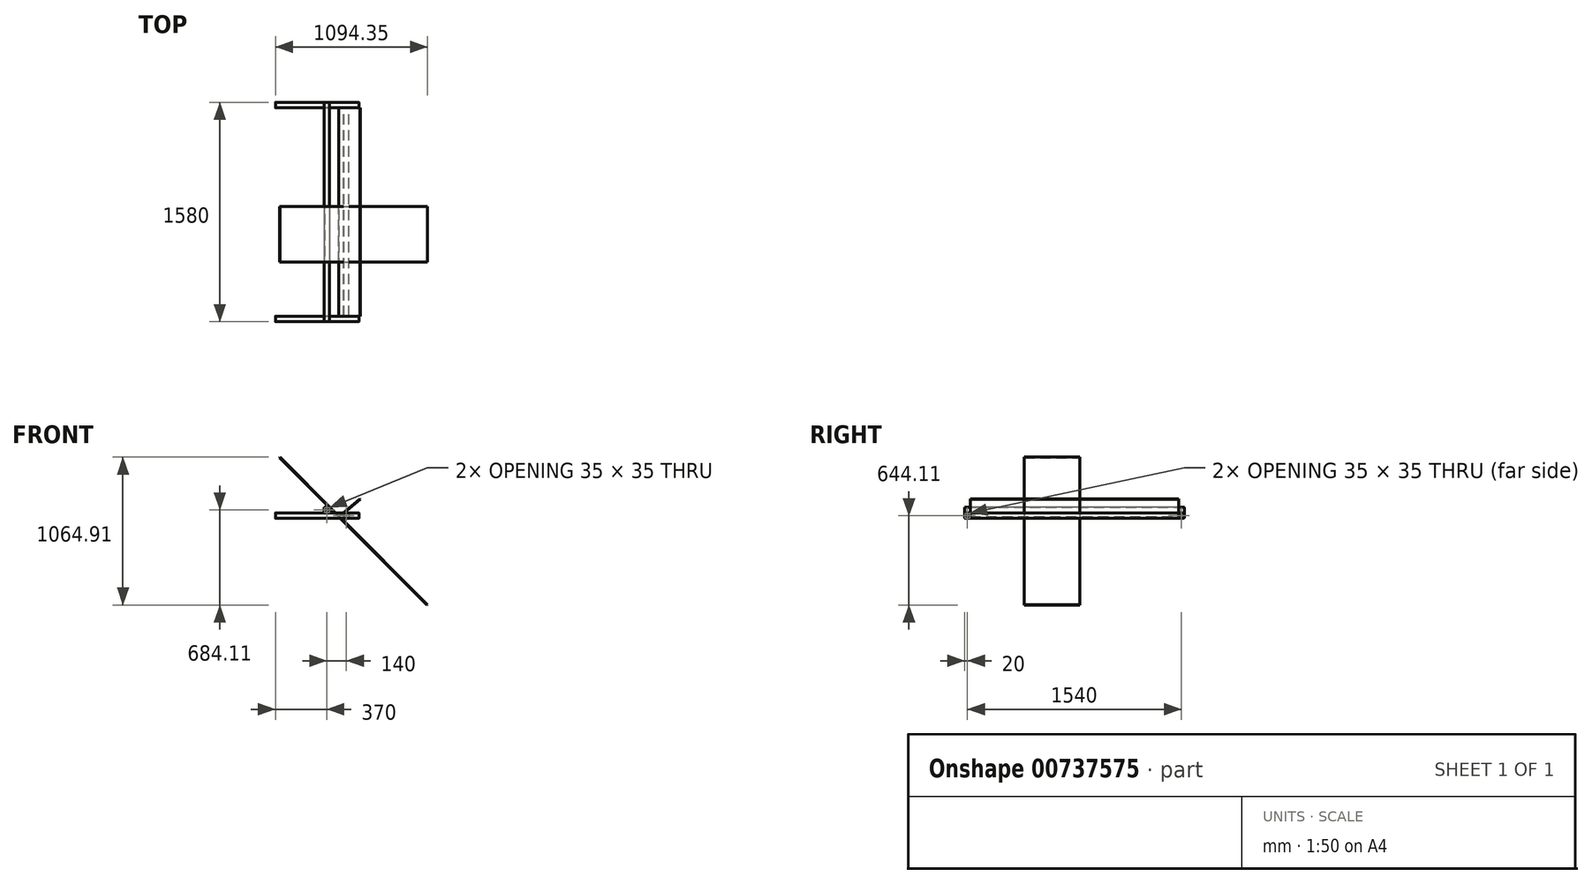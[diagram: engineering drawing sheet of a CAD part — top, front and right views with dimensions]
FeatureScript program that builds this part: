
annotation { "Feature Type Name" : "Feature", "Feature Type Description" : "" }
export const myFeature = defineFeature(function(context is Context, id is Id, definition is map)
    precondition{}
    {
        {
            var Q0;
            Q0=qCreatedBy(makeId("Right.planeOp"),FACE);
            var sketch = newSketch(context, id + "F0", { "sketchPlane" : qUnion([Q0])});
            skLineSegment(sketch, "E0.bottom", {"start": v(-504, 0) * mm, "end": v(-536, 0) * mm});
            skLineSegment(sketch, "E0.top", {"start": v(-504, 40) * mm, "end": v(-536, 40) * mm});
            skLineSegment(sketch, "E0.left", {"start": v(-500, 4) * mm, "end": v(-500, 36) * mm});
            skLineSegment(sketch, "E0.right", {"start": v(-540, 4) * mm, "end": v(-540, 36) * mm});
            skLineSegment(sketch, "E1.bottom", {"start": v(1004, 40) * mm, "end": v(1036, 40) * mm});
            skLineSegment(sketch, "E1.top", {"start": v(1004, 0) * mm, "end": v(1036, 0) * mm});
            skLineSegment(sketch, "E1.left", {"start": v(1000, 36) * mm, "end": v(1000, 4) * mm});
            skLineSegment(sketch, "E1.right", {"start": v(1040, 36) * mm, "end": v(1040, 4) * mm});
            skPoint(sketch, "E2.visualSharp", {"position": v(-500, 40) * mm});
            skArc(sketch, "E2.filletArc", {"start": v(-500, 36) * mm, "mid": v(-501.17, 38.83) * mm, "end": v(-504, 40) * mm});
            skPoint(sketch, "E3.visualSharp", {"position": v(-500, 0) * mm});
            skArc(sketch, "E3.filletArc", {"start": v(-504, 0) * mm, "mid": v(-501.17, 1.17) * mm, "end": v(-500, 4) * mm});
            skPoint(sketch, "E4.visualSharp", {"position": v(-540, 40) * mm});
            skArc(sketch, "E4.filletArc", {"start": v(-536, 40) * mm, "mid": v(-538.83, 38.83) * mm, "end": v(-540, 36) * mm});
            skPoint(sketch, "E5.visualSharp", {"position": v(-540, 0) * mm});
            skArc(sketch, "E5.filletArc", {"start": v(-540, 4) * mm, "mid": v(-538.83, 1.17) * mm, "end": v(-536, 0) * mm});
            skPoint(sketch, "E6.visualSharp", {"position": v(1040, 40) * mm});
            skArc(sketch, "E6.filletArc", {"start": v(1040, 36) * mm, "mid": v(1038.83, 38.83) * mm, "end": v(1036, 40) * mm});
            skPoint(sketch, "E7.visualSharp", {"position": v(1040, 0) * mm});
            skArc(sketch, "E7.filletArc", {"start": v(1036, 0) * mm, "mid": v(1038.83, 1.17) * mm, "end": v(1040, 4) * mm});
            skPoint(sketch, "E8.visualSharp", {"position": v(1000, 0) * mm});
            skArc(sketch, "E8.filletArc", {"start": v(1000, 4) * mm, "mid": v(1001.17, 1.17) * mm, "end": v(1004, 0) * mm});
            skPoint(sketch, "E9.visualSharp", {"position": v(1000, 40) * mm});
            skArc(sketch, "E9.filletArc", {"start": v(1004, 40) * mm, "mid": v(1001.17, 38.83) * mm, "end": v(1000, 36) * mm});
            skSolve(sketch);
        }
        {
            var Q0;
            Q0=makeQuery(id+"F0.imprint","IMPRINT",FACE,{"disambiguationData":[TD([[makeQuery(id+"F0.imprint","IMPRINT",EDGE,{"derivedFrom":sQuery(id+"F0.wireOp",EDGE,"E0.bottom")}),-1.0]])]});
            var Q1;
            Q1=makeQuery(id+"F0.imprint","IMPRINT",FACE,{"disambiguationData":[TD([[makeQuery(id+"F0.imprint","IMPRINT",EDGE,{"derivedFrom":sQuery(id+"F0.wireOp",EDGE,"E1.bottom")}),-1.0]])]});
            extrude(context, id + "F1", {"entities" : qUnion([Q0, Q1]), "endBound" : BoundingType.SYMMETRIC, "depth" : 600 * mm, "offsetDistance" : 25 * mm});
        }
        {
            var Q0;
            Q0=makeQuery(id+"F1.opExtrude","CAP_FACE",FACE,{"disambiguationData":[OSD([sQuery(id+"F0.wireOp",EDGE,"E0.bottom"),sQuery(id+"F0.wireOp",EDGE,"E0.top"),sQuery(id+"F0.wireOp",EDGE,"E0.left"),sQuery(id+"F0.wireOp",EDGE,"E0.right"),sQuery(id+"F0.wireOp",EDGE,"E2.filletArc"),sQuery(id+"F0.wireOp",EDGE,"E3.filletArc"),sQuery(id+"F0.wireOp",EDGE,"E4.filletArc"),sQuery(id+"F0.wireOp",EDGE,"E5.filletArc")])],"isStart":false});
            var Q1;
            Q1=makeQuery(id+"F1.opExtrude","CAP_FACE",FACE,{"disambiguationData":[OSD([sQuery(id+"F0.wireOp",EDGE,"E1.bottom"),sQuery(id+"F0.wireOp",EDGE,"E1.top"),sQuery(id+"F0.wireOp",EDGE,"E1.left"),sQuery(id+"F0.wireOp",EDGE,"E1.right"),sQuery(id+"F0.wireOp",EDGE,"E6.filletArc"),sQuery(id+"F0.wireOp",EDGE,"E7.filletArc"),sQuery(id+"F0.wireOp",EDGE,"E8.filletArc"),sQuery(id+"F0.wireOp",EDGE,"E9.filletArc")])],"isStart":false});
            var Q2;
            Q2=makeQuery(id+"F1.opExtrude","SWEPT_BODY",BODY,{"disambiguationData":[OSD([sQuery(id+"F0.wireOp",EDGE,"E0.bottom"),sQuery(id+"F0.wireOp",EDGE,"E0.top"),sQuery(id+"F0.wireOp",EDGE,"E0.left"),sQuery(id+"F0.wireOp",EDGE,"E0.right"),sQuery(id+"F0.wireOp",EDGE,"E2.filletArc"),sQuery(id+"F0.wireOp",EDGE,"E3.filletArc"),sQuery(id+"F0.wireOp",EDGE,"E4.filletArc"),sQuery(id+"F0.wireOp",EDGE,"E5.filletArc")])]});
            shell(context, id + "F2", {"entities" : qUnion([Q0, Q1]), "parts" : qUnion([Q2]), "thickness" : 2.5 * mm});
        }
        {
            var Q0;
            Q0=makeQuery(id+"F1.opExtrude","CAP_FACE",FACE,{"disambiguationData":[OSD([sQuery(id+"F0.wireOp",EDGE,"E0.bottom"),sQuery(id+"F0.wireOp",EDGE,"E0.top"),sQuery(id+"F0.wireOp",EDGE,"E0.left"),sQuery(id+"F0.wireOp",EDGE,"E0.right"),sQuery(id+"F0.wireOp",EDGE,"E2.filletArc"),sQuery(id+"F0.wireOp",EDGE,"E3.filletArc"),sQuery(id+"F0.wireOp",EDGE,"E4.filletArc"),sQuery(id+"F0.wireOp",EDGE,"E5.filletArc")])],"isStart":false});
            var sketch = newSketch(context, id + "F3", { "sketchPlane" : qUnion([Q0])});
            skArc(sketch, "E10.0.0", {"start": v(-502.5, 36) * mm, "mid": v(-502.94, 37.06) * mm, "end": v(-504, 37.5) * mm});
            skLineSegment(sketch, "E10.0.1", {"start": v(-504, 37.5) * mm, "end": v(-536, 37.5) * mm});
            skArc(sketch, "E10.0.2", {"start": v(-536, 37.5) * mm, "mid": v(-537.06, 37.06) * mm, "end": v(-537.5, 36) * mm});
            skLineSegment(sketch, "E10.0.3", {"start": v(-537.5, 36) * mm, "end": v(-537.5, 4) * mm});
            skArc(sketch, "E10.0.4", {"start": v(-537.5, 4) * mm, "mid": v(-537.06, 2.94) * mm, "end": v(-536, 2.5) * mm});
            skLineSegment(sketch, "E10.0.5", {"start": v(-536, 2.5) * mm, "end": v(-504, 2.5) * mm});
            skArc(sketch, "E10.0.6", {"start": v(-504, 2.5) * mm, "mid": v(-502.94, 2.94) * mm, "end": v(-502.5, 4) * mm});
            skLineSegment(sketch, "E10.0.7", {"start": v(-502.5, 4) * mm, "end": v(-502.5, 36) * mm});
            skArc(sketch, "E11.0.0", {"start": v(1002.5, 4) * mm, "mid": v(1002.94, 2.94) * mm, "end": v(1004, 2.5) * mm});
            skLineSegment(sketch, "E11.0.1", {"start": v(1004, 2.5) * mm, "end": v(1036, 2.5) * mm});
            skArc(sketch, "E11.0.2", {"start": v(1036, 2.5) * mm, "mid": v(1037.06, 2.94) * mm, "end": v(1037.5, 4) * mm});
            skLineSegment(sketch, "E11.0.3", {"start": v(1037.5, 4) * mm, "end": v(1037.5, 36) * mm});
            skArc(sketch, "E11.0.4", {"start": v(1037.5, 36) * mm, "mid": v(1037.06, 37.06) * mm, "end": v(1036, 37.5) * mm});
            skLineSegment(sketch, "E11.0.5", {"start": v(1036, 37.5) * mm, "end": v(1004, 37.5) * mm});
            skArc(sketch, "E11.0.6", {"start": v(1004, 37.5) * mm, "mid": v(1002.94, 37.06) * mm, "end": v(1002.5, 36) * mm});
            skLineSegment(sketch, "E11.0.7", {"start": v(1002.5, 36) * mm, "end": v(1002.5, 4) * mm});
            skSolve(sketch);
        }
        {
            var Q0;
            Q0=makeQuery(id+"F3.imprint","IMPRINT",FACE,{"disambiguationData":[TD([[makeQuery(id+"F3.imprint","IMPRINT",EDGE,{"derivedFrom":sQuery(id+"F3.wireOp",EDGE,"E11.0.0")}),1.0]])]});
            var Q1;
            Q1=makeQuery(id+"F3.imprint","IMPRINT",FACE,{"disambiguationData":[TD([[makeQuery(id+"F3.imprint","IMPRINT",EDGE,{"derivedFrom":sQuery(id+"F3.wireOp",EDGE,"E10.0.0")}),1.0]])]});
            extrude(context, id + "F4", {"entities" : qUnion([Q0, Q1]), "operationType" : NewBodyOperationType.REMOVE, "oppositeDirection" : true, "depth" : 1000 * mm, "offsetDistance" : 25 * mm});
        }
        {
            var Q0;
            Q0=makeQuery(id+"F1.opExtrude","SWEPT_FACE",FACE,{"disambiguationData":[OSD([sQuery(id+"F0.wireOp",EDGE,"E0.right")])]});
            var sketch = newSketch(context, id + "F5", { "sketchPlane" : qUnion([Q0])});
            skLineSegment(sketch, "E12.0", {"start": v(86, 40) * mm, "end": v(54, 40) * mm});
            skLineSegment(sketch, "E13.bottom", {"start": v(-147.4, 40) * mm, "end": v(-107.4, 40) * mm});
            skLineSegment(sketch, "E13.top", {"start": v(54, 80) * mm, "end": v(86, 80) * mm});
            skLineSegment(sketch, "E13.left", {"start": v(50, 44) * mm, "end": v(50, 76) * mm});
            skLineSegment(sketch, "E13.right", {"start": v(90, 44) * mm, "end": v(90, 76) * mm});
            skPoint(sketch, "E14.visualSharp", {"position": v(90, 80) * mm});
            skArc(sketch, "E14.filletArc", {"start": v(90, 76) * mm, "mid": v(88.83, 78.83) * mm, "end": v(86, 80) * mm});
            skPoint(sketch, "E15.newPointB", {"position": v(300, 40) * mm});
            skArc(sketch, "E15.filletArc", {"start": v(86, 40) * mm, "mid": v(88.83, 41.17) * mm, "end": v(90, 44) * mm});
            skPoint(sketch, "E16.visualSharp", {"position": v(50, 80) * mm});
            skArc(sketch, "E16.filletArc", {"start": v(54, 80) * mm, "mid": v(51.17, 78.83) * mm, "end": v(50, 76) * mm});
            skPoint(sketch, "E17.newPointB", {"position": v(-300, 40) * mm});
            skArc(sketch, "E17.filletArc", {"start": v(50, 44) * mm, "mid": v(51.17, 41.17) * mm, "end": v(54, 40) * mm});
            skLineSegment(sketch, "E18.bottom", {"start": v(54.5, 77.5) * mm, "end": v(85.5, 77.5) * mm});
            skLineSegment(sketch, "E18.top", {"start": v(54.5, 42.5) * mm, "end": v(85.5, 42.5) * mm});
            skLineSegment(sketch, "E18.left", {"start": v(52.5, 75.5) * mm, "end": v(52.5, 44.5) * mm});
            skLineSegment(sketch, "E18.right", {"start": v(87.5, 75.5) * mm, "end": v(87.5, 44.5) * mm});
            skPoint(sketch, "E19.visualSharp", {"position": v(52.5, 77.5) * mm});
            skArc(sketch, "E19.filletArc", {"start": v(54.5, 77.5) * mm, "mid": v(53.09, 76.91) * mm, "end": v(52.5, 75.5) * mm});
            skPoint(sketch, "E20.visualSharp", {"position": v(87.5, 77.5) * mm});
            skArc(sketch, "E20.filletArc", {"start": v(87.5, 75.5) * mm, "mid": v(86.91, 76.91) * mm, "end": v(85.5, 77.5) * mm});
            skPoint(sketch, "E21.visualSharp", {"position": v(87.5, 42.5) * mm});
            skArc(sketch, "E21.filletArc", {"start": v(85.5, 42.5) * mm, "mid": v(86.91, 43.09) * mm, "end": v(87.5, 44.5) * mm});
            skPoint(sketch, "E22.visualSharp", {"position": v(52.5, 42.5) * mm});
            skArc(sketch, "E22.filletArc", {"start": v(52.5, 44.5) * mm, "mid": v(53.09, 43.09) * mm, "end": v(54.5, 42.5) * mm});
            skSolve(sketch);
        }
        {
            var Q0;
            Q0=makeQuery(id+"F5.imprint","IMPRINT",FACE,{"disambiguationData":[TD([[makeQuery(id+"F5.imprint","IMPRINT",EDGE,{"derivedFrom":sQuery(id+"F5.wireOp",EDGE,"E13.top")}),-1.0]])]});
            var Q1;
            Q1=makeQuery(id+"F1.opExtrude","SWEPT_FACE",FACE,{"disambiguationData":[OSD([sQuery(id+"F0.wireOp",EDGE,"E1.right")])]});
            extrude(context, id + "F6", {"entities" : qUnion([Q0]), "endBound" : BoundingType.UP_TO_SURFACE, "oppositeDirection" : true, "depth" : 25 * mm, "endBoundEntityFace" : qUnion([Q1]), "offsetDistance" : 25 * mm});
        }
        {
            var Q0;
            Q0=makeQuery(id+"F1.opExtrude","SWEPT_FACE",FACE,{"disambiguationData":[OSD([sQuery(id+"F0.wireOp",EDGE,"E1.left")])]});
            var sketch = newSketch(context, id + "F7", { "sketchPlane" : qUnion([Q0])});
            skLineSegment(sketch, "E23.0", {"start": v(226, 40) * mm, "end": v(194, 40) * mm});
            skLineSegment(sketch, "E24.0", {"start": v(300, 36) * mm, "end": v(-300, 36) * mm});
            skLineSegment(sketch, "E25.bottom", {"start": v(71.03, 40) * mm, "end": v(109.03, 40) * mm});
            skLineSegment(sketch, "E25.top", {"start": v(194, 0) * mm, "end": v(226, 0) * mm});
            skLineSegment(sketch, "E25.left", {"start": v(190, 36) * mm, "end": v(190, 4) * mm});
            skLineSegment(sketch, "E25.right", {"start": v(230, 36) * mm, "end": v(230, 4) * mm});
            skPoint(sketch, "E26.newPointA", {"position": v(-300, 40) * mm});
            skArc(sketch, "E26.filletArc", {"start": v(194, 40) * mm, "mid": v(191.17, 38.83) * mm, "end": v(190, 36) * mm});
            skPoint(sketch, "E27.newPointB", {"position": v(300, 40) * mm});
            skArc(sketch, "E27.filletArc", {"start": v(230, 36) * mm, "mid": v(228.83, 38.83) * mm, "end": v(226, 40) * mm});
            skPoint(sketch, "E28.visualSharp", {"position": v(230, 0) * mm});
            skArc(sketch, "E28.filletArc", {"start": v(226, 0) * mm, "mid": v(228.83, 1.17) * mm, "end": v(230, 4) * mm});
            skPoint(sketch, "E29.visualSharp", {"position": v(190, 0) * mm});
            skArc(sketch, "E29.filletArc", {"start": v(190, 4) * mm, "mid": v(191.17, 1.17) * mm, "end": v(194, 0) * mm});
            skLineSegment(sketch, "E30.bottom", {"start": v(194.5, 37.5) * mm, "end": v(225.5, 37.5) * mm});
            skLineSegment(sketch, "E30.top", {"start": v(194.5, 2.5) * mm, "end": v(225.5, 2.5) * mm});
            skLineSegment(sketch, "E30.left", {"start": v(192.5, 35.5) * mm, "end": v(192.5, 4.5) * mm});
            skLineSegment(sketch, "E30.right", {"start": v(227.5, 35.5) * mm, "end": v(227.5, 4.5) * mm});
            skPoint(sketch, "E31.visualSharp", {"position": v(192.5, 37.5) * mm});
            skArc(sketch, "E31.filletArc", {"start": v(194.5, 37.5) * mm, "mid": v(193.09, 36.91) * mm, "end": v(192.5, 35.5) * mm});
            skPoint(sketch, "E32.visualSharp", {"position": v(227.5, 37.5) * mm});
            skArc(sketch, "E32.filletArc", {"start": v(227.5, 35.5) * mm, "mid": v(226.91, 36.91) * mm, "end": v(225.5, 37.5) * mm});
            skPoint(sketch, "E33.visualSharp", {"position": v(227.5, 2.5) * mm});
            skArc(sketch, "E33.filletArc", {"start": v(225.5, 2.5) * mm, "mid": v(226.91, 3.09) * mm, "end": v(227.5, 4.5) * mm});
            skPoint(sketch, "E34.visualSharp", {"position": v(192.5, 2.5) * mm});
            skArc(sketch, "E34.filletArc", {"start": v(192.5, 4.5) * mm, "mid": v(193.09, 3.09) * mm, "end": v(194.5, 2.5) * mm});
            skSolve(sketch);
        }
        {
            var Q0;
            {var subQ0=sQuery(id+"F7.wireOp",EDGE,"E26.filletArc");Q0=makeQuery(id+"F7.imprint","IMPRINT",FACE,{"disambiguationData":[TD([[makeQuery(id+"F7.imprint","IMPRINT",EDGE,{"derivedFrom":subQ0}),1.0]])]});}
            var Q1;
            {var subQ1=sQuery(id+"F7.wireOp",EDGE,"E25.left");Q1=makeQuery(id+"F7.imprint","IMPRINT",FACE,{"disambiguationData":[TD([[makeQuery(id+"F7.imprint","IMPRINT",EDGE,{"derivedFrom":subQ1}),1.0]])]});}
            var Q2;
            Q2=makeQuery(id+"F7.imprint","IMPRINT",FACE,{"disambiguationData":[TD([[makeQuery(id+"F7.imprint","IMPRINT",EDGE,{"derivedFrom":sQuery(id+"F7.wireOp",EDGE,"E25.top")}),1.0]])]});
            var Q3;
            {var subQ4=sQuery(id+"F7.wireOp",EDGE,"E25.right");Q3=makeQuery(id+"F7.imprint","IMPRINT",FACE,{"disambiguationData":[TD([[makeQuery(id+"F7.imprint","IMPRINT",EDGE,{"derivedFrom":subQ4}),-1.0]])]});}
            var Q4;
            Q4=makeQuery(id+"F1.opExtrude","SWEPT_FACE",FACE,{"disambiguationData":[OSD([sQuery(id+"F0.wireOp",EDGE,"E0.left")])]});
            extrude(context, id + "F8", {"entities" : qUnion([Q0, Q1, Q2, Q3]), "endBound" : BoundingType.UP_TO_SURFACE, "depth" : 25 * mm, "endBoundEntityFace" : qUnion([Q4]), "offsetDistance" : 25 * mm});
        }
        {
            var Q0;
            Q0=makeQuery(id+"F6.opExtrude","SWEPT_EDGE",EDGE,{"disambiguationData":[OSD([sQuery(id+"F5.wireOp",EDGE,"E13.right"),sQuery(id+"F5.wireOp",EDGE,"E14.filletArc")])]});
            cPlane(context, id + "F9", {"entities" : qUnion([Q0]), "cplaneType" : CPlaneType.LINE_ANGLE, "offset" : 25 * mm, "angle" : 45 * degree, "oppositeDirection" : true, "width" : 150 * mm, "height" : 150 * mm});
        }
        {
            var Q0;
            Q0=qCreatedBy(id+"F9.planeOp",FACE);
            var sketch = newSketch(context, id + "F10", { "sketchPlane" : qUnion([Q0])});
            skLineSegment(sketch, "E35.0", {"start": v(186.68, 500) * mm, "end": v(-237.59, 500) * mm});
            skLineSegment(sketch, "E36.0", {"start": v(186.68, -1000) * mm, "end": v(-237.59, -1000) * mm});
            skLineSegment(sketch, "E37.bottom", {"start": v(-290.1, 500) * mm, "end": v(109.9, 500) * mm});
            skLineSegment(sketch, "E37.top", {"start": v(-290.1, -1000) * mm, "end": v(109.9, -1000) * mm});
            skLineSegment(sketch, "E37.left", {"start": v(-290.1, 500) * mm, "end": v(-290.1, -1000) * mm});
            skLineSegment(sketch, "E37.right", {"start": v(109.9, 500) * mm, "end": v(109.9, -1000) * mm});
            skSolve(sketch);
        }
        {
            var Q0;
            Q0=makeQuery(id+"F8.opExtrude","SWEPT_EDGE",EDGE,{"disambiguationData":[OSD([sQuery(id+"F7.wireOp",EDGE,"E24.0"),sQuery(id+"F7.wireOp",EDGE,"E25.left"),sQuery(id+"F7.wireOp",EDGE,"E26.filletArc")])]});
            cPlane(context, id + "F11", {"entities" : qUnion([Q0]), "cplaneType" : CPlaneType.LINE_ANGLE, "offset" : 25 * mm, "angle" : 40 * degree, "oppositeDirection" : true, "width" : 150 * mm, "height" : 150 * mm});
        }
        {
            var Q0;
            Q0=qCreatedBy(id+"F11.planeOp",FACE);
            var sketch = newSketch(context, id + "F12", { "sketchPlane" : qUnion([Q0])});
            skLineSegment(sketch, "E38.0", {"start": v(126.51, -500) * mm, "end": v(126.51, 1000) * mm});
            skLineSegment(sketch, "E39.0", {"start": v(252.95, 1000) * mm, "end": v(-206.67, 1000) * mm});
            skLineSegment(sketch, "E40.0", {"start": v(255.52, -504) * mm, "end": v(-204.1, -504) * mm});
            skLineSegment(sketch, "E41.bottom", {"start": v(326.51, 1000) * mm, "end": v(126.51, 1000) * mm});
            skLineSegment(sketch, "E41.top", {"start": v(326.51, -500) * mm, "end": v(126.51, -500) * mm});
            skLineSegment(sketch, "E41.left", {"start": v(326.51, 1000) * mm, "end": v(326.51, -500) * mm});
            skLineSegment(sketch, "E41.right", {"start": v(126.51, 1000) * mm, "end": v(126.51, -500) * mm});
            skSolve(sketch);
        }
        {
            var Q0;
            {var subQ2=sQuery(id+"F10.wireOp",EDGE,"E37.left");Q0=makeQuery(id+"F10.imprint","IMPRINT",FACE,{"disambiguationData":[TD([[makeQuery(id+"F10.imprint","IMPRINT",EDGE,{"derivedFrom":subQ2}),1.0]])]});}
            extrude(context, id + "F13", {"entities" : qUnion([Q0]), "oppositeDirection" : true, "depth" : 6 * mm, "offsetDistance" : 25 * mm});
        }
        {
            var Q0;
            Q0=makeQuery(id+"F12.imprint","IMPRINT",FACE,{"disambiguationData":[TD([[makeQuery(id+"F12.imprint","IMPRINT",EDGE,{"derivedFrom":sQuery(id+"F12.wireOp",EDGE,"E41.top")}),-1.0]])]});
            extrude(context, id + "F14", {"entities" : qUnion([Q0]), "depth" : 5 * mm, "offsetDistance" : 25 * mm});
        }
    });
